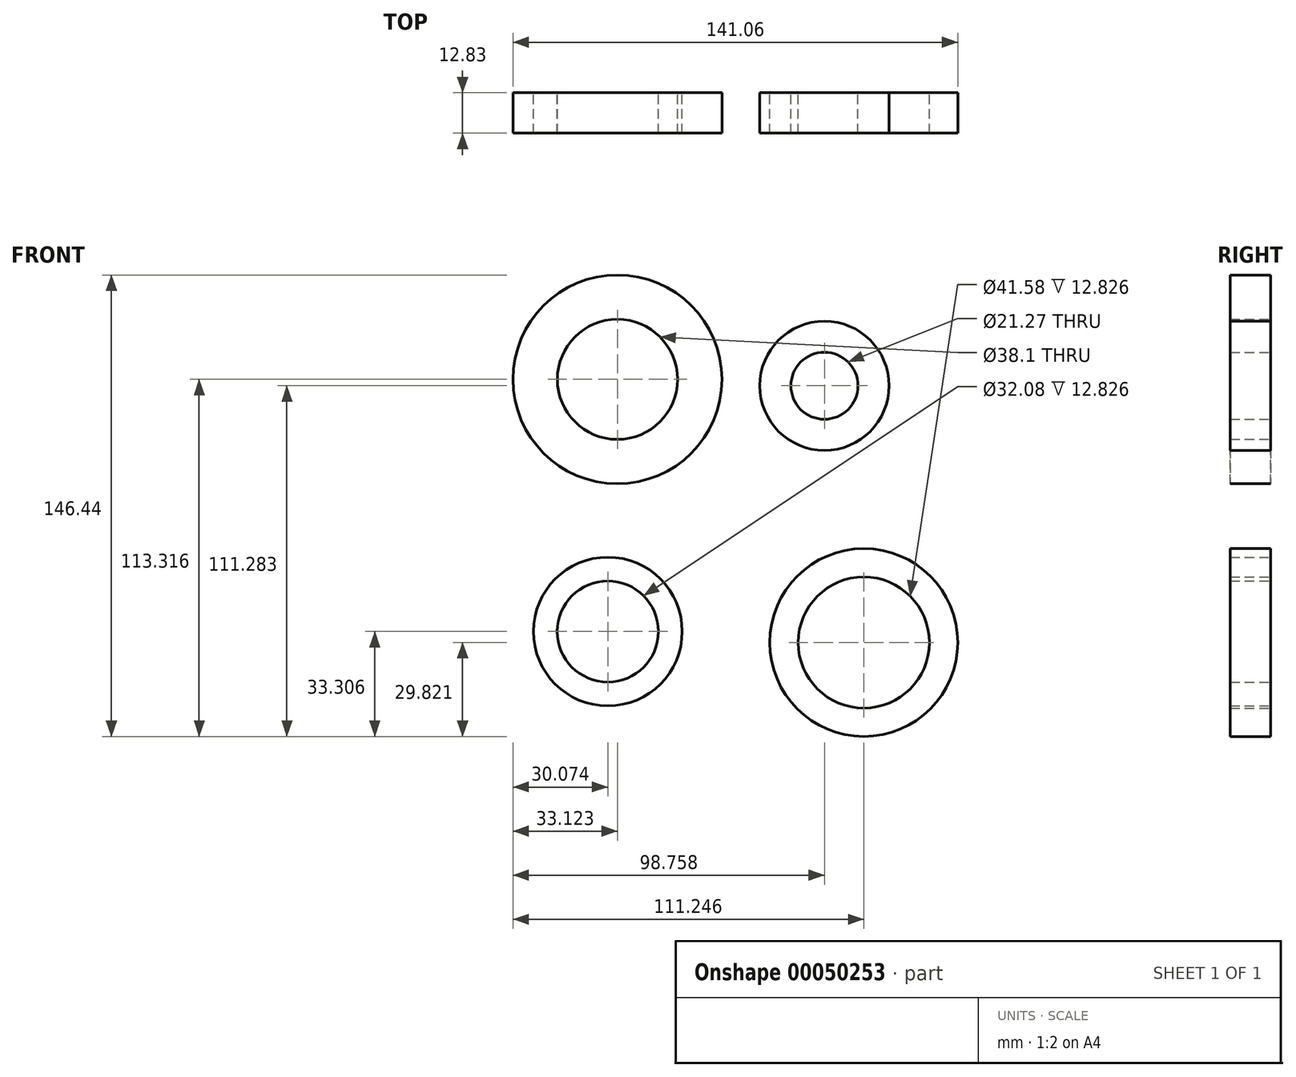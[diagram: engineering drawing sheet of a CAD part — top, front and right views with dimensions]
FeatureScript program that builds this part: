
annotation { "Feature Type Name" : "Feature", "Feature Type Description" : "" }
export const myFeature = defineFeature(function(context is Context, id is Id, definition is map)
    precondition{}
    {
        {
            var Q0;
            Q0=qCreatedBy(makeId("Front.planeOp"),FACE);
            var sketch = newSketch(context, id + "F0", { "sketchPlane" : qUnion([Q0])});
            skCircle(sketch, "E0", {"center": v(-44.5, 35.58) * mm, "radius": 33.12 * mm});
            skCircle(sketch, "E1", {"center": v(-44.5, 35.58) * mm, "radius": 19.05 * mm});
            skCircle(sketch, "E2", {"center": v(21.13, 33.54) * mm, "radius": 20.5 * mm});
            skCircle(sketch, "E3", {"center": v(21.13, 33.54) * mm, "radius": 10.64 * mm});
            skCircle(sketch, "E4", {"center": v(-47.56, -44.43) * mm, "radius": 23.59 * mm});
            skCircle(sketch, "E5", {"center": v(-47.56, -44.43) * mm, "radius": 16.04 * mm});
            skCircle(sketch, "E6", {"center": v(33.62, -47.92) * mm, "radius": 29.82 * mm});
            skCircle(sketch, "E7", {"center": v(33.62, -47.92) * mm, "radius": 20.8 * mm});
            skSolve(sketch);
        }
        {
            var Q0;
            Q0=makeQuery(id+"F0.imprint","IMPRINT",FACE,{"disambiguationData":[TD([[makeQuery(id+"F0.imprint","IMPRINT",EDGE,{"derivedFrom":sQuery(id+"F0.wireOp",EDGE,"E2")}),1.0]])]});
            var Q1;
            Q1=makeQuery(id+"F0.imprint","IMPRINT",FACE,{"disambiguationData":[TD([[makeQuery(id+"F0.imprint","IMPRINT",EDGE,{"derivedFrom":sQuery(id+"F0.wireOp",EDGE,"E6")}),1.0]])]});
            var Q2;
            Q2=makeQuery(id+"F0.imprint","IMPRINT",FACE,{"disambiguationData":[TD([[makeQuery(id+"F0.imprint","IMPRINT",EDGE,{"derivedFrom":sQuery(id+"F0.wireOp",EDGE,"E0")}),1.0]])]});
            var Q3;
            Q3=makeQuery(id+"F0.imprint","IMPRINT",FACE,{"disambiguationData":[TD([[makeQuery(id+"F0.imprint","IMPRINT",EDGE,{"derivedFrom":sQuery(id+"F0.wireOp",EDGE,"E4")}),1.0]])]});
            extrude(context, id + "F1", {"entities" : qUnion([Q0, Q1, Q2, Q3]), "depth" : 12.83 * mm});
        }
    });
